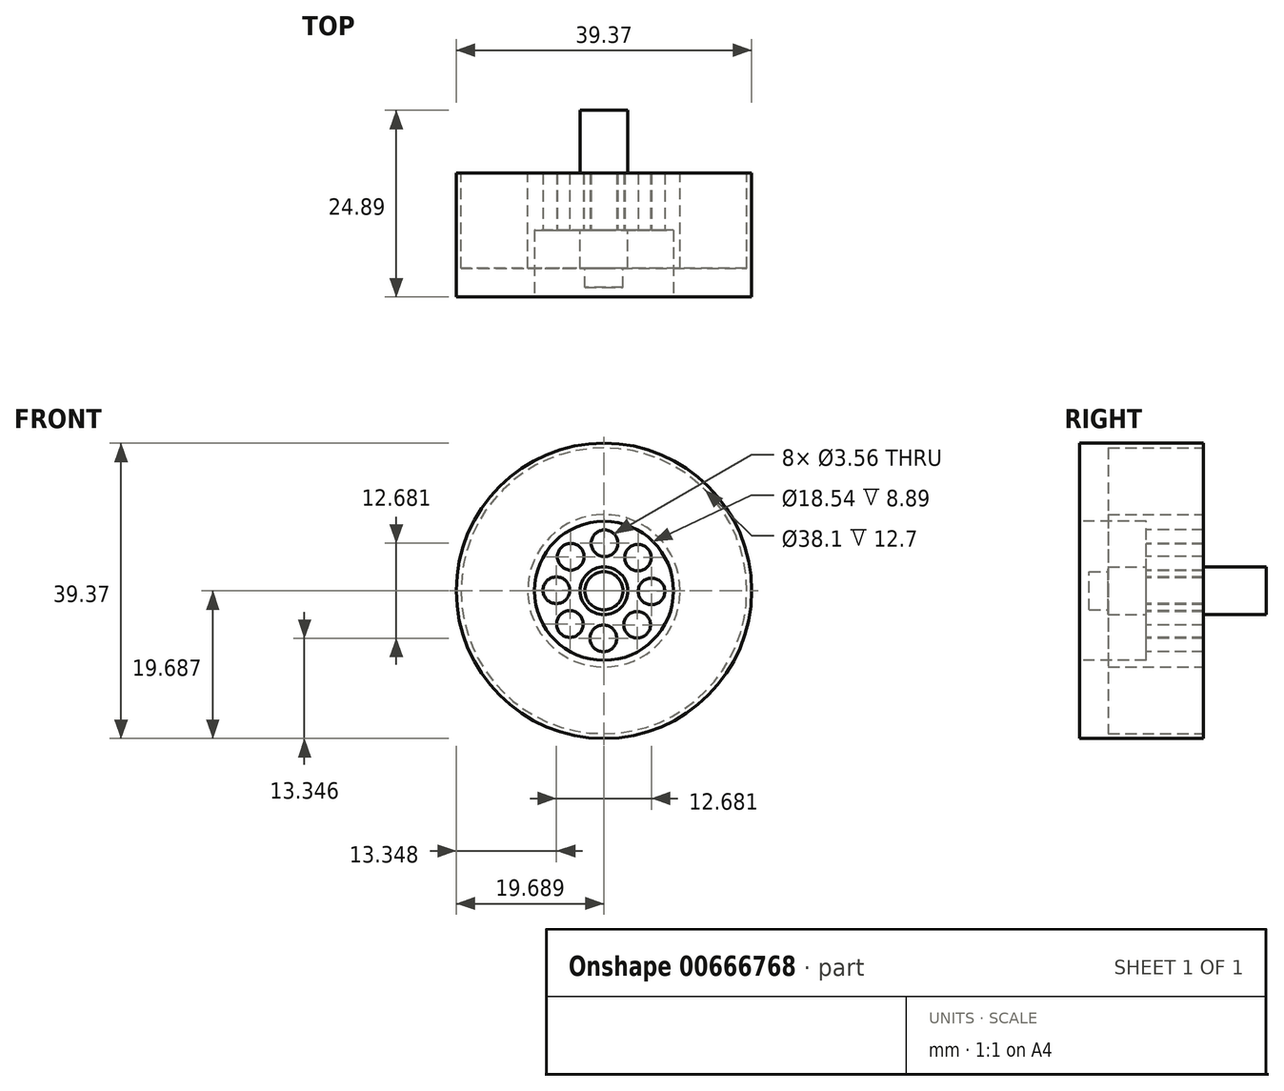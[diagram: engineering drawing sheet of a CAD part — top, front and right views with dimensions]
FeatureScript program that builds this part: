
annotation { "Feature Type Name" : "Feature", "Feature Type Description" : "" }
export const myFeature = defineFeature(function(context is Context, id is Id, definition is map)
    precondition{}
    {
        {
            var Q0;
            Q0=qCreatedBy(makeId("Front.planeOp"),FACE);
            var sketch = newSketch(context, id + "F0", { "sketchPlane" : qUnion([Q0])});
            skCircle(sketch, "E0", {"center": v(-28.32, 34.42) * mm, "radius": 19.69 * mm});
            skCircle(sketch, "E1", {"center": v(-28.32, 34.42) * mm, "radius": 8.9 * mm});
            skCircle(sketch, "E2", {"center": v(-28.32, 34.42) * mm, "radius": 10.16 * mm});
            skSolve(sketch);
        }
        {
            var Q0;
            Q0=makeQuery(id+"F0.imprint","IMPRINT",FACE,{"disambiguationData":[TD([[makeQuery(id+"F0.imprint","IMPRINT",EDGE,{"derivedFrom":sQuery(id+"F0.wireOp",EDGE,"E0")}),1.0]])]});
            var Q1;
            Q1=makeQuery(id+"F0.imprint","IMPRINT",FACE,{"disambiguationData":[TD([[makeQuery(id+"F0.imprint","IMPRINT",EDGE,{"derivedFrom":sQuery(id+"F0.wireOp",EDGE,"E1")}),-1.0]])]});
            var Q2;
            Q2=makeQuery(id+"F0.imprint","IMPRINT",FACE,{"disambiguationData":[TD([[makeQuery(id+"F0.imprint","IMPRINT",EDGE,{"derivedFrom":sQuery(id+"F0.wireOp",EDGE,"E1")}),1.0]])]});
            extrude(context, id + "F1", {"entities" : qUnion([Q0, Q1, Q2]), "depth" : 24.9 * mm, "offsetDistance" : 25.4 * mm});
        }
        {
            var Q0;
            Q0=makeQuery(id+"F1.opExtrude","CAP_FACE",FACE,{"disambiguationData":[OSD([sQuery(id+"F0.wireOp",EDGE,"E0")])],"isStart":true});
            var sketch = newSketch(context, id + "F2", { "sketchPlane" : qUnion([Q0])});
            skCircle(sketch, "E3", {"center": v(28.32, 34.42) * mm, "radius": 3.18 * mm});
            skSolve(sketch);
        }
        {
            var Q0;
            Q0=makeQuery(id+"F2.imprint","IMPRINT",FACE,{"disambiguationData":[TD([[makeQuery(id+"F2.imprint","IMPRINT",EDGE,{"derivedFrom":sQuery(id+"F2.wireOp",EDGE,"E3")}),-1.0]])]});
            extrude(context, id + "F3", {"entities" : qUnion([Q0]), "operationType" : NewBodyOperationType.REMOVE, "oppositeDirection" : true, "depth" : 8.38 * mm, "offsetDistance" : 25.4 * mm});
        }
        {
            var Q0;
            Q0=makeQuery(id+"F1.opExtrude","CAP_FACE",FACE,{"disambiguationData":[OSD([sQuery(id+"F0.wireOp",EDGE,"E0")])],"isStart":false});
            var sketch = newSketch(context, id + "F4", { "sketchPlane" : qUnion([Q0])});
            skCircle(sketch, "E4", {"center": v(-28.32, 34.42) * mm, "radius": 9.27 * mm});
            skSolve(sketch);
        }
        {
            var Q0;
            Q0=makeQuery(id+"F4.imprint","IMPRINT",FACE,{"disambiguationData":[TD([[makeQuery(id+"F4.imprint","IMPRINT",EDGE,{"derivedFrom":sQuery(id+"F4.wireOp",EDGE,"E4")}),1.0]])]});
            extrude(context, id + "F5", {"entities" : qUnion([Q0]), "operationType" : NewBodyOperationType.REMOVE, "oppositeDirection" : true, "depth" : 8.9 * mm, "offsetDistance" : 25.4 * mm});
        }
        {
            var Q0;
            Q0=makeQuery(id+"F5.boolean.opBoolean","COPY",FACE,{"derivedFrom":makeQuery(id+"F5.opExtrude","CAP_FACE",FACE,{"disambiguationData":[OSD([sQuery(id+"F4.wireOp",EDGE,"E4")])],"isStart":false})});
            var sketch = newSketch(context, id + "F6", { "sketchPlane" : qUnion([Q0])});
            skCircle(sketch, "E5", {"center": v(-28.32, 34.42) * mm, "radius": 3.18 * mm});
            skSolve(sketch);
        }
        {
            var Q0;
            Q0=makeQuery(id+"F6.imprint","IMPRINT",FACE,{"disambiguationData":[TD([[makeQuery(id+"F6.imprint","IMPRINT",EDGE,{"derivedFrom":sQuery(id+"F6.wireOp",EDGE,"E5")}),1.0]])]});
            extrude(context, id + "F7", {"entities" : qUnion([Q0]), "operationType" : NewBodyOperationType.ADD, "depth" : 5.08 * mm, "offsetDistance" : 25.4 * mm});
        }
        {
            var Q0;
            Q0=makeQuery(id+"F5.boolean.opBoolean","COPY",FACE,{"derivedFrom":makeQuery(id+"F5.opExtrude","CAP_FACE",FACE,{"disambiguationData":[OSD([sQuery(id+"F4.wireOp",EDGE,"E4")])],"isStart":false})});
            var sketch = newSketch(context, id + "F8", { "sketchPlane" : qUnion([Q0])});
            skCircle(sketch, "E6", {"center": v(-28.24, 40.76) * mm, "radius": 1.78 * mm});
            skCircle(sketch, "E7.1.0", {"center": v(-32.75, 38.96) * mm, "radius": 1.78 * mm});
            skCircle(sketch, "E7.2.0", {"center": v(-34.66, 34.5) * mm, "radius": 1.78 * mm});
            skCircle(sketch, "E7.3.0", {"center": v(-32.86, 29.99) * mm, "radius": 1.78 * mm});
            skCircle(sketch, "E7.4.0", {"center": v(-28.4, 28.08) * mm, "radius": 1.78 * mm});
            skCircle(sketch, "E7.5.0", {"center": v(-23.9, 29.88) * mm, "radius": 1.78 * mm});
            skCircle(sketch, "E7.6.0", {"center": v(-21.98, 34.34) * mm, "radius": 1.78 * mm});
            skCircle(sketch, "E7.7.0", {"center": v(-23.78, 38.85) * mm, "radius": 1.78 * mm});
            skPoint(sketch, "E7.center", {"position": v(-28.32, 34.42) * mm});
            skSolve(sketch);
        }
        {
            var Q0;
            Q0=makeQuery(id+"F8.imprint","IMPRINT",FACE,{"disambiguationData":[TD([[makeQuery(id+"F8.imprint","IMPRINT",EDGE,{"derivedFrom":sQuery(id+"F8.wireOp",EDGE,"E7.1.0")}),1.0]])]});
            var Q1;
            Q1=makeQuery(id+"F8.imprint","IMPRINT",FACE,{"disambiguationData":[TD([[makeQuery(id+"F8.imprint","IMPRINT",EDGE,{"derivedFrom":sQuery(id+"F8.wireOp",EDGE,"E6")}),1.0]])]});
            var Q2;
            Q2=makeQuery(id+"F8.imprint","IMPRINT",FACE,{"disambiguationData":[TD([[makeQuery(id+"F8.imprint","IMPRINT",EDGE,{"derivedFrom":sQuery(id+"F8.wireOp",EDGE,"E7.7.0")}),1.0]])]});
            var Q3;
            Q3=makeQuery(id+"F8.imprint","IMPRINT",FACE,{"disambiguationData":[TD([[makeQuery(id+"F8.imprint","IMPRINT",EDGE,{"derivedFrom":sQuery(id+"F8.wireOp",EDGE,"E7.6.0")}),1.0]])]});
            var Q4;
            Q4=makeQuery(id+"F8.imprint","IMPRINT",FACE,{"disambiguationData":[TD([[makeQuery(id+"F8.imprint","IMPRINT",EDGE,{"derivedFrom":sQuery(id+"F8.wireOp",EDGE,"E7.5.0")}),1.0]])]});
            var Q5;
            Q5=makeQuery(id+"F8.imprint","IMPRINT",FACE,{"disambiguationData":[TD([[makeQuery(id+"F8.imprint","IMPRINT",EDGE,{"derivedFrom":sQuery(id+"F8.wireOp",EDGE,"E7.4.0")}),1.0]])]});
            var Q6;
            Q6=makeQuery(id+"F8.imprint","IMPRINT",FACE,{"disambiguationData":[TD([[makeQuery(id+"F8.imprint","IMPRINT",EDGE,{"derivedFrom":sQuery(id+"F8.wireOp",EDGE,"E7.3.0")}),1.0]])]});
            var Q7;
            Q7=makeQuery(id+"F8.imprint","IMPRINT",FACE,{"disambiguationData":[TD([[makeQuery(id+"F8.imprint","IMPRINT",EDGE,{"derivedFrom":sQuery(id+"F8.wireOp",EDGE,"E7.2.0")}),1.0]])]});
            extrude(context, id + "F9", {"entities" : qUnion([Q0, Q1, Q2, Q3, Q4, Q5, Q6, Q7]), "operationType" : NewBodyOperationType.REMOVE, "oppositeDirection" : true, "depth" : 7.75 * mm, "offsetDistance" : 25.4 * mm});
        }
        {
            var Q0;
            Q0=makeQuery(id+"F7.opExtrude","CAP_FACE",FACE,{"disambiguationData":[OSD([sQuery(id+"F6.wireOp",EDGE,"E5")])],"isStart":false});
            var sketch = newSketch(context, id + "F10", { "sketchPlane" : qUnion([Q0])});
            skCircle(sketch, "E8", {"center": v(-28.32, 34.42) * mm, "radius": 2.54 * mm});
            skSolve(sketch);
        }
        {
            var Q0;
            Q0=makeQuery(id+"F10.imprint","IMPRINT",FACE,{"disambiguationData":[TD([[makeQuery(id+"F10.imprint","IMPRINT",EDGE,{"derivedFrom":sQuery(id+"F10.wireOp",EDGE,"E8")}),1.0]])]});
            extrude(context, id + "F11", {"entities" : qUnion([Q0]), "operationType" : NewBodyOperationType.ADD, "depth" : 2.54 * mm, "offsetDistance" : 25.4 * mm});
        }
        {
            var Q0;
            Q0=makeQuery(id+"F3.boolean.opBoolean","COPY",FACE,{"derivedFrom":makeQuery(id+"F3.opExtrude","CAP_FACE",FACE,{"disambiguationData":[OSD([sQuery(id+"F0.wireOp",EDGE,"E0"),sQuery(id+"F2.wireOp",EDGE,"E3")])],"isStart":false})});
            var sketch = newSketch(context, id + "F12", { "sketchPlane" : qUnion([Q0])});
            skCircle(sketch, "E9", {"center": v(28.32, 34.42) * mm, "radius": 10.16 * mm});
            skCircle(sketch, "E10", {"center": v(28.32, 34.42) * mm, "radius": 19.05 * mm});
            skSolve(sketch);
        }
        {
            var Q0;
            Q0 = qSketchRegion(id + "F12", true);
            extrude(context, id + "F13", {"entities" : qUnion([Q0]), "operationType" : NewBodyOperationType.REMOVE, "oppositeDirection" : true, "depth" : 12.7 * mm, "offsetDistance" : 25.4 * mm});
        }
    });
